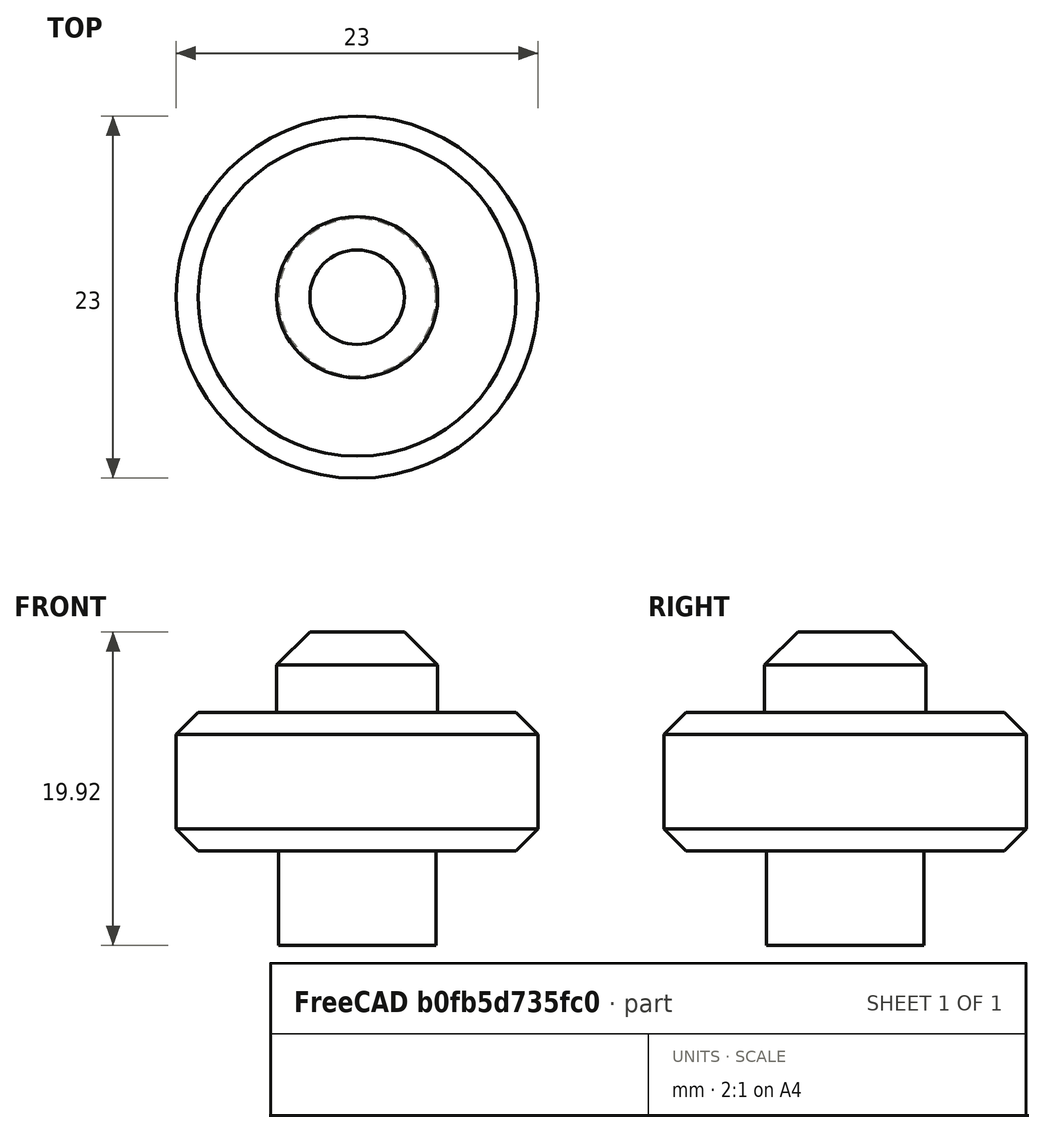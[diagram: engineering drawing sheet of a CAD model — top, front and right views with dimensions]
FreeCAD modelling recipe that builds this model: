
FCSTD DOCUMENT  (FreeCAD 0.20R29410 (Git))
Label: GantryWheel
License: All rights reserved
LicenseURL: http://en.wikipedia.org/wiki/All_rights_reserved
objects: App::DocumentObjectGroup×3, PartDesign::CoordinateSystem×1, App::FeaturePython×1, Sketcher::SketchObject×1, PartDesign::Revolution×1, PartDesign::Body×1, App::Part×1
note: 5 computed .brp shape members not serialized (recipe doc carries the construction recipe); baked Part::Feature solids carry a one-line shape summary decoded from their .brp

FEATURE [App::DocumentObjectGroup] Parts
FEATURE [PartDesign::CoordinateSystem] LCS_Origin
  AttacherType = Attacher::AttachEngine3D
  MapMode = 2
  Support = -> [X_Axis]
FEATURE [App::FeaturePython] Variables  # WARN: FeaturePython — macro-defined, semantics opaque (R4)
  Type = App::PropertyContainer
FEATURE [App::DocumentObjectGroup] Constraints
FEATURE [App::DocumentObjectGroup] Configurations
FEATURE [Sketcher::SketchObject] Sketch
  FullyConstrained = true
  MapMode = 5
  Placement = pos=(0,0,0) rot=(1,0,0;1.5708rad)
  Support = -> [XZ_Plane001]
  sketch-geometry (11):
    g0: LineSegment StartX=0 StartY=19.9213 StartZ=0 EndX=3 EndY=19.9213 EndZ=0
    g1: LineSegment StartX=3 StartY=19.9213 StartZ=0 EndX=5.12132 EndY=17.8 EndZ=0
    g2: LineSegment StartX=5.12132 StartY=17.8 StartZ=0 EndX=5.12132 EndY=14.8 EndZ=0
    g3: LineSegment StartX=5.12132 StartY=14.8 StartZ=0 EndX=10.1 EndY=14.8 EndZ=0
    g4: LineSegment StartX=10.1 StartY=14.8 StartZ=0 EndX=11.5 EndY=13.4 EndZ=0
    g5: LineSegment StartX=11.5 StartY=13.4 StartZ=0 EndX=11.5 EndY=7.4 EndZ=0
    g6: LineSegment StartX=11.5 StartY=7.4 StartZ=0 EndX=10.1 EndY=6 EndZ=0
    g7: LineSegment StartX=10.1 StartY=6 StartZ=0 EndX=5 EndY=6 EndZ=0
    g8: LineSegment StartX=5 StartY=6 StartZ=0 EndX=5 EndY=0 EndZ=0
    g9: LineSegment StartX=5 StartY=0 StartZ=0 EndX=0 EndY=0 EndZ=0
    g10: LineSegment StartX=0 StartY=0 StartZ=0 EndX=0 EndY=19.9213 EndZ=0
  constraints (32):
    c: PointOnObject(g0,g-2)
    c: Horizontal(g0)
    c: Coincident(g0,g1)
    c: Coincident(g1,g2)
    c: Vertical(g2)
    c: Coincident(g2,g3)
    c: Horizontal(g3)
    c: Coincident(g3,g4)
    c: Coincident(g4,g5)
    c: Vertical(g5)
    c: Coincident(g5,g6)
    c: Coincident(g6,g7)
    c: Horizontal(g7)
    c: Coincident(g7,g8)
    c: Vertical(g8)
    c: PointOnObject(g9,g-1)
    c: Coincident(g9,g-1)
    c: Coincident(g9,g10)
    c: Coincident(g10,g0)
    c: Equal(g6,g4)
    c: DistanceY(g5,g5) = 6
    c: Angle(g6,g7) = 2.35619
    c: Angle(g3,g4) = 2.35619
    c: DistanceY(g6,g3) = 8.8
    c: Angle(g1,g2) = 2.35619
    c: Equal(g2,g1)
    c: Equal(g1,g0)
    c: DistanceX(g0,g0) = 3
    c: Coincident(g9,g8)
    c: DistanceY(g8,g8) = 6
    c: DistanceX(g9,g9) = 5
    c: DistanceX(g9,g5) = 11.5
FEATURE [PartDesign::Revolution] Revolution
  Angle = 360
  Axis = (0,-2e-16,1)
  Base = (0,0,0)
  Placement = pos=(0,0,0) rot=(1,0,0;1.5708rad)
  Profile = -> Sketch
  ReferenceAxis = -> Sketch [V_Axis]
  Reversed = true
FEATURE [PartDesign::Body] Body
  Group = -> [Sketch,Revolution]
  Origin = -> Origin001
  Tip = -> Revolution
FEATURE [App::Part] Assembly
  AssemblyType = Part::Link
  Group = -> [LCS_Origin,Variables,Constraints,Configurations,Body]
  Origin = -> Origin
  Type = Assembly
